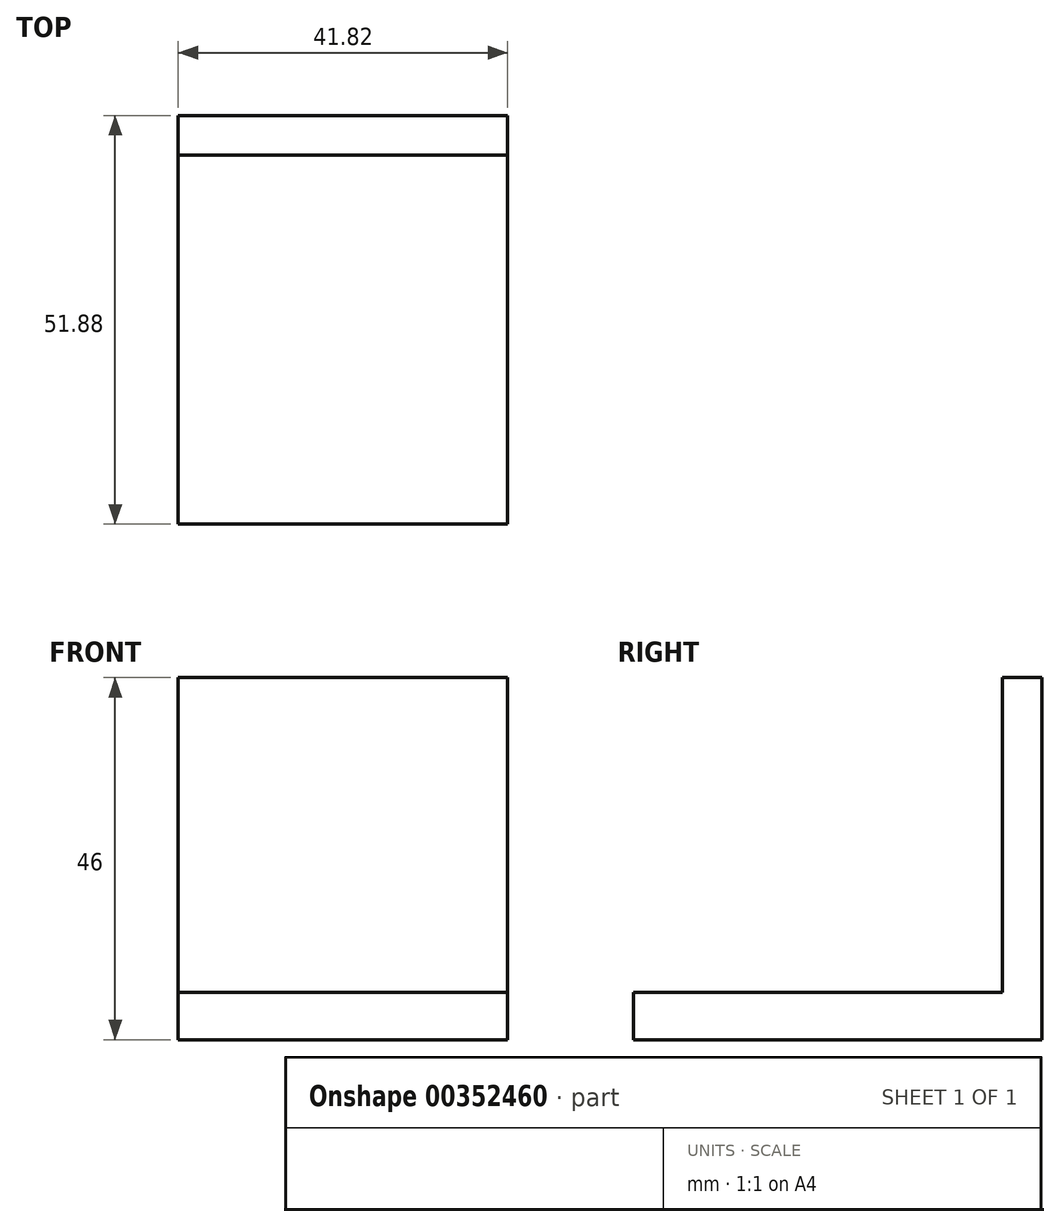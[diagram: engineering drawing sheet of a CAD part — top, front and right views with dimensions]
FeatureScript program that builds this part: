
annotation { "Feature Type Name" : "Feature", "Feature Type Description" : "" }
export const myFeature = defineFeature(function(context is Context, id is Id, definition is map)
    precondition{}
    {
        {
            var Q0;
            Q0=qCreatedBy(makeId("Front.planeOp"),FACE);
            var sketch = newSketch(context, id + "F0", { "sketchPlane" : qUnion([Q0])});
            skLineSegment(sketch, "E0.bottom", {"start": v(20.9, 23) * mm, "end": v(-20.9, 23) * mm});
            skLineSegment(sketch, "E0.top", {"start": v(20.9, -23) * mm, "end": v(-20.9, -23) * mm});
            skLineSegment(sketch, "E0.left", {"start": v(20.9, 23) * mm, "end": v(20.9, -23) * mm});
            skLineSegment(sketch, "E0.right", {"start": v(-20.9, 23) * mm, "end": v(-20.9, -23) * mm});
            skPoint(sketch, "E0.middle", {"position": v(0, 0) * mm});
            skSolve(sketch);
        }
        {
            var Q0;
            Q0=makeQuery(id+"F0.imprint","IMPRINT",FACE,{"disambiguationData":[TD([[makeQuery(id+"F0.imprint","IMPRINT",EDGE,{"derivedFrom":sQuery(id+"F0.wireOp",EDGE,"E0.bottom")}),1.0]])]});
            extrude(context, id + "F1", {"entities" : qUnion([Q0]), "depth" : 5 * mm});
        }
        {
            var Q0;
            Q0=makeQuery(id+"F1.opExtrude","SWEPT_FACE",FACE,{"disambiguationData":[OSD([sQuery(id+"F0.wireOp",EDGE,"E0.top")])]});
            var sketch = newSketch(context, id + "F2", { "sketchPlane" : qUnion([Q0])});
            skLineSegment(sketch, "E1.bottom", {"start": v(-20.9, 5) * mm, "end": v(20.9, 5) * mm});
            skLineSegment(sketch, "E1.top", {"start": v(-20.9, 5) * mm, "end": v(20.9, 5) * mm});
            skLineSegment(sketch, "E1.left", {"start": v(-20.9, 5) * mm, "end": v(-20.9, 5) * mm});
            skLineSegment(sketch, "E1.right", {"start": v(20.9, 5) * mm, "end": v(20.9, 5) * mm});
            skLineSegment(sketch, "E2.top", {"start": v(-20.9, 51.88) * mm, "end": v(20.9, 51.88) * mm});
            skLineSegment(sketch, "E2.left", {"start": v(-20.9, 5) * mm, "end": v(-20.9, 51.88) * mm});
            skLineSegment(sketch, "E2.right", {"start": v(20.9, 5) * mm, "end": v(20.9, 51.88) * mm});
            skSolve(sketch);
        }
        {
            var Q0;
            Q0 = qSketchRegion(id + "F2", true);
            extrude(context, id + "F3", {"entities" : qUnion([Q0]), "operationType" : NewBodyOperationType.ADD, "oppositeDirection" : true, "depth" : 6 * mm});
        }
    });
